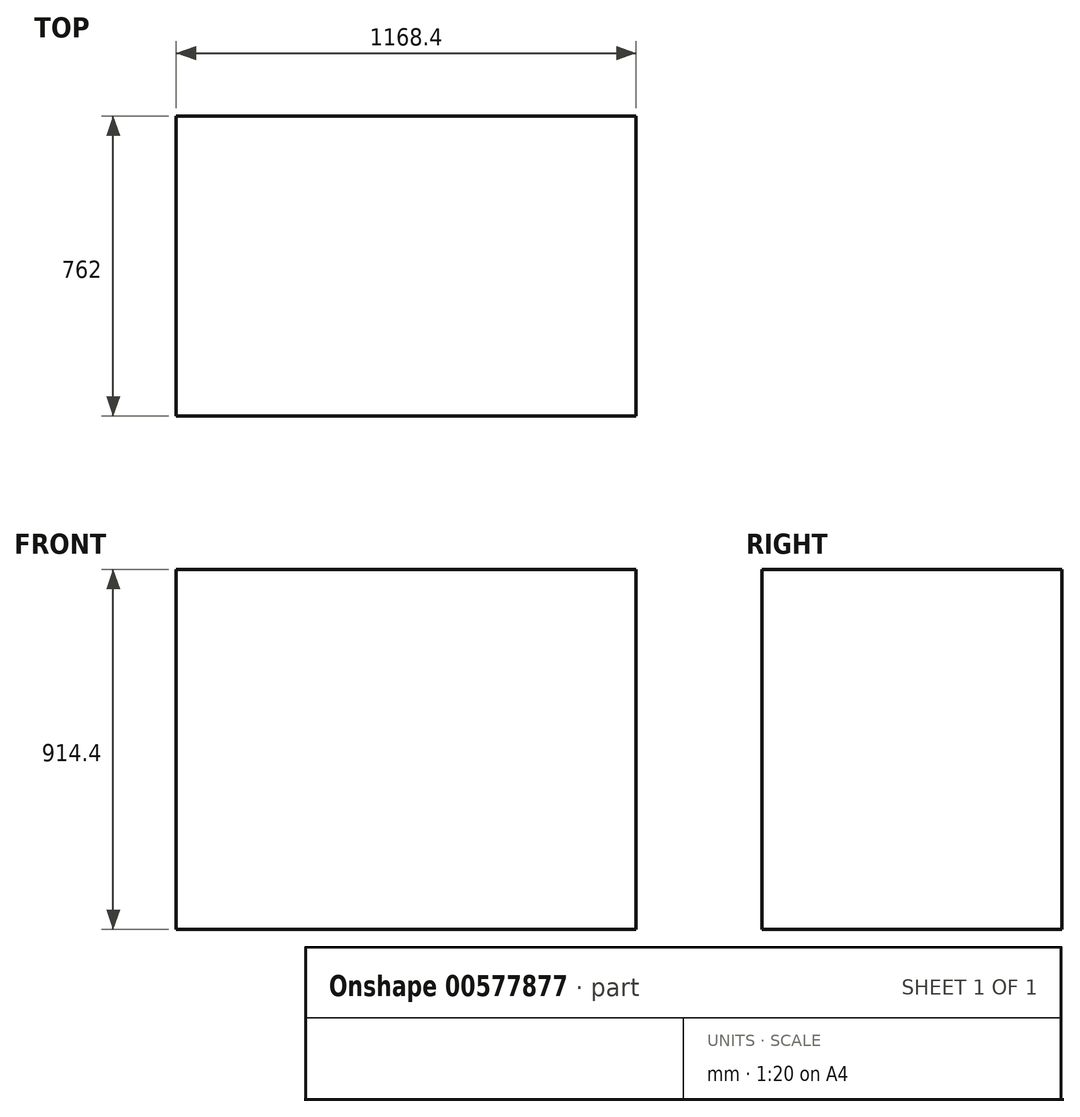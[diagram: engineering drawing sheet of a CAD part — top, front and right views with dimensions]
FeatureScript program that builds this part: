
annotation { "Feature Type Name" : "Feature", "Feature Type Description" : "" }
export const myFeature = defineFeature(function(context is Context, id is Id, definition is map)
    precondition{}
    {
        {
            var Q0;
            Q0=qCreatedBy(makeId("Top.planeOp"),FACE);
            var sketch = newSketch(context, id + "F0", { "sketchPlane" : qUnion([Q0])});
            skLineSegment(sketch, "E0.bottom", {"start": v(-584.2, -381) * mm, "end": v(584.2, -381) * mm});
            skLineSegment(sketch, "E0.top", {"start": v(-584.2, 381) * mm, "end": v(584.2, 381) * mm});
            skLineSegment(sketch, "E0.left", {"start": v(-584.2, -381) * mm, "end": v(-584.2, 381) * mm});
            skLineSegment(sketch, "E0.right", {"start": v(584.2, -381) * mm, "end": v(584.2, 381) * mm});
            skPoint(sketch, "E0.middle", {"position": v(0, 0) * mm});
            skSolve(sketch);
        }
        {
            var Q0;
            Q0=makeQuery(id+"F0.imprint","IMPRINT",FACE,{"disambiguationData":[TD([[makeQuery(id+"F0.imprint","IMPRINT",EDGE,{"derivedFrom":sQuery(id+"F0.wireOp",EDGE,"E0.bottom")}),1.0]])]});
            extrude(context, id + "F1", {"entities" : qUnion([Q0]), "depth" : 914.4 * mm, "offsetDistance" : 25.4 * mm});
        }
    });
